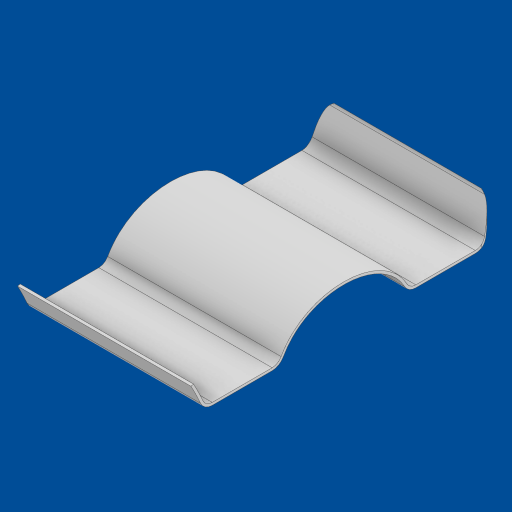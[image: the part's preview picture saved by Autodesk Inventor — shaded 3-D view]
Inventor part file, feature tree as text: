
AUTODESK INVENTOR PART (.ipt)
format: ipt  version: 2023.1 (Build 271208000, 208)  size: 214,528 bytes
history: native  units: mm
features: other x1, extrude x1, split x1, sketch x1
ambient origin geometry x8: Origin, YZ Plane, XZ Plane, XY Plane, X Axis, Y Axis, Z Axis, Center Point
bodies: Solid1 (feature_tree)
feature tree (4):
  other  "top_case.ipt"
  extrude  "Extrusion1"  Depth=10.0mm
  split  "Split1"
  sketch  "Sketch13"  dims[d0=10.0mm d1=1.0mm d2=70.0mm d3=0.0mm]
